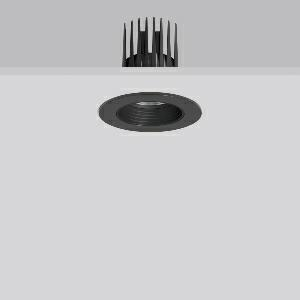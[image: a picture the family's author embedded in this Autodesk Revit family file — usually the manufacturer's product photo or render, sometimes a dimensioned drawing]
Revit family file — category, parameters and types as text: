
# Revit family: heledon_mini_e_901744_003_2_c190
name_source: partatom
category: Lighting Fixtures
units: mm (PartAtom-declared; Revit-internal decimal feet)

## family parameters
Cut with Voids When Loaded = No
Host = Face
Light Source = No
Part Type = Normal
Room Calculation Point = No
Round Connector Dimension = Use Diameter
Shared = No

## types (1)
- HELEDON mini E (1 x LED Modul 927, 2000 lm, 2700)
    Apparent Load = 20 VA
    Approval mark = CE
    CIE Flux Codes = 96 100 100 100 100
    Color Rendering = 92
    Color Temperature = 2700
    Default Elevation = 1800 mm
    Description = Series: HELEDON mini
Round recessed downlight. Housing: die-cast aluminium, powder-coated. Black plastic ring and recessed LED to prevent glare from the side. Optical assembly with lens made of plastic (polycarbonate) for the best homogeneous light distribution - can be changed without tools. Best colour rendering index Ra>90. Suitable for Recessed ceiling mounting. Installation without tools thanks to spring fastening system. Including separate LED converter with connecting cable 600 mm.High quality converter without flickering and stroboscopic effect. Through-wiring box (5 pole) available as accessory. The following accessories can be mounted without use of tools: interchangeable lenses, decorative glasses, honeycomb louvre, clear and frosted diffusers, white interchangeable plastic ring. 
Colour: deep black, matt (RAL 9005)
Diameter: 124 mm
Height: 3 mm
Cut-out diameter: 114 mm
Recess height: 170 mm
Luminaire: recess height: 120 mm
Lamp: LED
Socket: without socket
Colour temperature: 2700K
Colour rendering index (CRI): 92
System power: 20 W
Rated luminous flux: 2000 lm
Luminous efficiency: 100 lm/W
Control gear: Regulated power supply
Protection class: II
Type of protection: IP 20
    Height = 0 mm  [stored 0 ft]
    Lamp = 1 x LED Modul 927
    Lamp Light Flux = 2000 lm
    Lamp count = 1
    Length = 124 mm  [stored 0.406824 ft]
    Lifetime = 50000 h
    Luminous efficacy = 100 lm/W
    Manufacturer = RZB
    ModVariant = No
    Model = 901744.003.2
    Mounting Place = Ceiling
    Mounting Type = Recessed
    Number of Poles = 1
    OnlyDefault = Yes
    Power Factor = 1
    Product Name = HELEDON mini E
    Product group = Recessed downlights
    ProductGroupID = 402
    Protection Class = Protection class II
    Protection Degree = IP 20
    RLX_Detail_Level = 1
    RLX_Emergency_Light_Flux = 0 lm
    RLX_Emergency_Type = 0
    RLX_Emergency_Type_DB = No
    RlxData = <blob elided: 127845 chars, md5=a6fbe173>
    Socket = socket
    Standby Power = 0 W
    System Light Flux = 2000 lm
    System Power = 20 W
    Type Comments = Product without accessories
    Type Image = 901656.003.jpg
    URL = http://relux.com
    VarID = ---
    Voltage = 230 V
    Voltage Range = 220-240 V
    Weight = 0.00 kg
    Width = 0 mm  [stored 0 ft]

note: [stored X ft] marks values corroborated as IEEE doubles in the binary element streams (Revit-internal decimal feet)

## geometry (parser evidence)
native form markers: Blend x4, Sweep x12
no freeform markers — native parametric forms only
